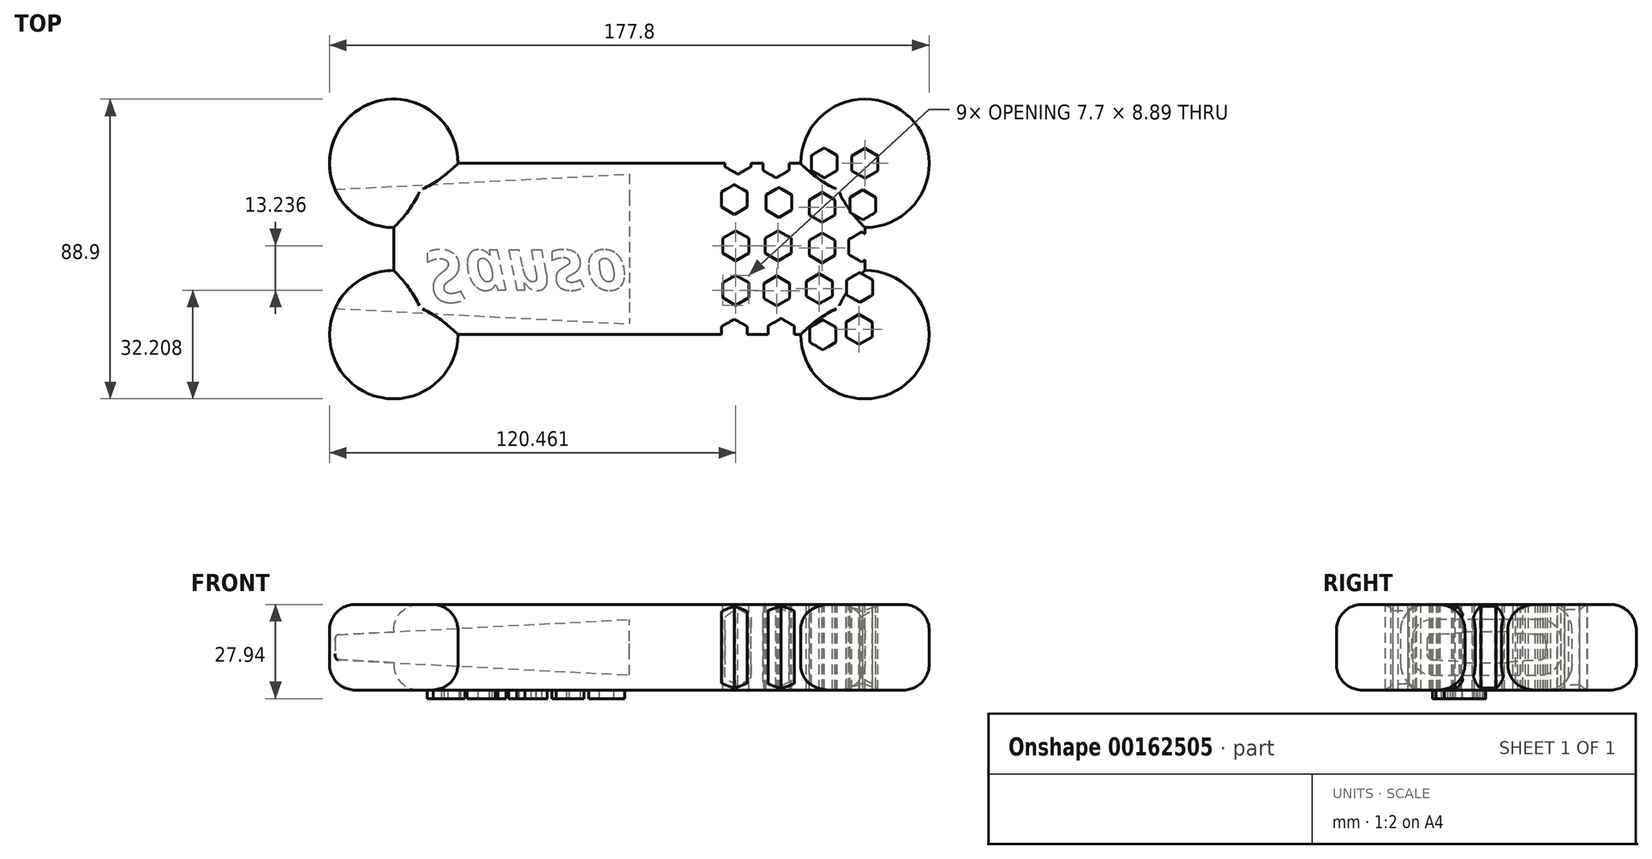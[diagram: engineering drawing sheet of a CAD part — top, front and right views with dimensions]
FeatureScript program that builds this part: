
annotation { "Feature Type Name" : "Feature", "Feature Type Description" : "" }
export const myFeature = defineFeature(function(context is Context, id is Id, definition is map)
    precondition{}
    {
        {
            var Q0;
            Q0=qCreatedBy(makeId("Top.planeOp"),FACE);
            var sketch = newSketch(context, id + "F0", { "sketchPlane" : qUnion([Q0])});
            skLineSegment(sketch, "E0.bottom", {"start": v(-50.8, 25.4) * mm, "end": v(50.8, 25.4) * mm});
            skLineSegment(sketch, "E0.top", {"start": v(-50.8, -25.4) * mm, "end": v(50.8, -25.4) * mm});
            skLineSegment(sketch, "E0.right", {"start": v(69.85, 6.35) * mm, "end": v(69.85, -6.35) * mm});
            skPoint(sketch, "E0.middle", {"position": v(0, 0) * mm});
            skArc(sketch, "E1", {"start": v(-50.8, 25.4) * mm, "mid": v(-83.32, 38.87) * mm, "end": v(-69.85, 6.35) * mm});
            skArc(sketch, "E2", {"start": v(50.8, -25.4) * mm, "mid": v(83.32, -38.87) * mm, "end": v(69.85, -6.35) * mm});
            skArc(sketch, "E3", {"start": v(69.85, 6.35) * mm, "mid": v(83.32, 38.87) * mm, "end": v(50.8, 25.4) * mm});
            skArc(sketch, "E4", {"start": v(-69.85, -6.35) * mm, "mid": v(-83.32, -38.87) * mm, "end": v(-50.8, -25.4) * mm});
            skLineSegment(sketch, "E5", {"start": v(-69.85, 6.35) * mm, "end": v(-69.85, -6.35) * mm});
            skSolve(sketch);
        }
        {
            var Q0;
            Q0 = qSketchRegion(id + "F0", true);
            extrude(context, id + "F1", {"entities" : qUnion([Q0]), "endBound" : BoundingType.SYMMETRIC, "depth" : 25.4 * mm});
        }
        {
            var Q0;
            Q0=makeQuery(id+"F1.opExtrude","CAP_EDGE",EDGE,{"disambiguationData":[OSD([sQuery(id+"F0.wireOp",EDGE,"E4")])],"isStart":false});
            var Q1;
            Q1=makeQuery(id+"F1.opExtrude","CAP_EDGE",EDGE,{"disambiguationData":[OSD([sQuery(id+"F0.wireOp",EDGE,"E5")])],"isStart":false});
            var Q2;
            Q2=makeQuery(id+"F1.opExtrude","CAP_EDGE",EDGE,{"disambiguationData":[OSD([sQuery(id+"F0.wireOp",EDGE,"E1")])],"isStart":false});
            var Q3;
            Q3=makeQuery(id+"F1.opExtrude","CAP_EDGE",EDGE,{"disambiguationData":[OSD([sQuery(id+"F0.wireOp",EDGE,"E4")])],"isStart":true});
            var Q4;
            Q4=makeQuery(id+"F1.opExtrude","CAP_EDGE",EDGE,{"disambiguationData":[OSD([sQuery(id+"F0.wireOp",EDGE,"E5")])],"isStart":true});
            var Q5;
            Q5=makeQuery(id+"F1.opExtrude","CAP_EDGE",EDGE,{"disambiguationData":[OSD([sQuery(id+"F0.wireOp",EDGE,"E1")])],"isStart":true});
            var Q6;
            Q6=makeQuery(id+"F1.opExtrude","CAP_EDGE",EDGE,{"disambiguationData":[OSD([sQuery(id+"F0.wireOp",EDGE,"E0.top")])],"isStart":false});
            var Q7;
            Q7=makeQuery(id+"F1.opExtrude","CAP_EDGE",EDGE,{"disambiguationData":[OSD([sQuery(id+"F0.wireOp",EDGE,"E0.bottom")])],"isStart":false});
            var Q8;
            Q8=makeQuery(id+"F1.opExtrude","CAP_EDGE",EDGE,{"disambiguationData":[OSD([sQuery(id+"F0.wireOp",EDGE,"E2")])],"isStart":false});
            var Q9;
            Q9=makeQuery(id+"F1.opExtrude","CAP_EDGE",EDGE,{"disambiguationData":[OSD([sQuery(id+"F0.wireOp",EDGE,"E0.right")])],"isStart":false});
            var Q10;
            Q10=makeQuery(id+"F1.opExtrude","CAP_EDGE",EDGE,{"disambiguationData":[OSD([sQuery(id+"F0.wireOp",EDGE,"E3")])],"isStart":false});
            var Q11;
            Q11=makeQuery(id+"F1.opExtrude","CAP_EDGE",EDGE,{"disambiguationData":[OSD([sQuery(id+"F0.wireOp",EDGE,"E0.right")])],"isStart":true});
            var Q12;
            Q12=makeQuery(id+"F1.opExtrude","CAP_EDGE",EDGE,{"disambiguationData":[OSD([sQuery(id+"F0.wireOp",EDGE,"E3")])],"isStart":true});
            var Q13;
            Q13=makeQuery(id+"F1.opExtrude","CAP_EDGE",EDGE,{"disambiguationData":[OSD([sQuery(id+"F0.wireOp",EDGE,"E2")])],"isStart":true});
            var Q14;
            Q14=makeQuery(id+"F1.opExtrude","CAP_EDGE",EDGE,{"disambiguationData":[OSD([sQuery(id+"F0.wireOp",EDGE,"E0.top")])],"isStart":true});
            var Q15;
            Q15=makeQuery(id+"F1.opExtrude","CAP_EDGE",EDGE,{"disambiguationData":[OSD([sQuery(id+"F0.wireOp",EDGE,"E0.bottom")])],"isStart":true});
            fillet(context, id + "F2", {"entities" : qUnion([Q0, Q1, Q2, Q3, Q4, Q5, Q6, Q7, Q8, Q9, Q10, Q11, Q12, Q13, Q14, Q15]), "radius" : 7.62 * mm, "tangentPropagation" : true, "allowEdgeOverflow" : false});
        }
        {
            var Q0;
            Q0=qCreatedBy(makeId("Right.planeOp"),FACE);
            var sketch = newSketch(context, id + "F3", { "sketchPlane" : qUnion([Q0])});
            skLineSegment(sketch, "E6.bottom", {"start": v(15.88, 8.26) * mm, "end": v(-15.88, 8.26) * mm});
            skLineSegment(sketch, "E6.top", {"start": v(15.88, -8.26) * mm, "end": v(-15.87, -8.26) * mm});
            skLineSegment(sketch, "E6.left", {"start": v(22.23, 1.9) * mm, "end": v(22.23, -1.9) * mm});
            skLineSegment(sketch, "E6.right", {"start": v(-22.23, 1.9) * mm, "end": v(-22.23, -1.9) * mm});
            skPoint(sketch, "E6.middle", {"position": v(0, 0) * mm});
            skPoint(sketch, "E7.visualSharp", {"position": v(22.23, 8.26) * mm});
            skArc(sketch, "E7.filletArc", {"start": v(22.23, 1.9) * mm, "mid": v(20.37, 6.4) * mm, "end": v(15.88, 8.26) * mm});
            skPoint(sketch, "E8.visualSharp", {"position": v(22.23, -8.26) * mm});
            skArc(sketch, "E8.filletArc", {"start": v(15.88, -8.26) * mm, "mid": v(20.37, -6.4) * mm, "end": v(22.23, -1.9) * mm});
            skPoint(sketch, "E9.visualSharp", {"position": v(-22.23, 8.26) * mm});
            skArc(sketch, "E9.filletArc", {"start": v(-15.88, 8.26) * mm, "mid": v(-20.37, 6.4) * mm, "end": v(-22.23, 1.9) * mm});
            skPoint(sketch, "E10.visualSharp", {"position": v(-22.23, -8.26) * mm});
            skArc(sketch, "E10.filletArc", {"start": v(-22.23, -1.9) * mm, "mid": v(-20.37, -6.4) * mm, "end": v(-15.87, -8.26) * mm});
            skSolve(sketch);
        }
        {
            var Q0;
            Q0 = qSketchRegion(id + "F3", true);
            extrude(context, id + "F4", {"entities" : qUnion([Q0]), "operationType" : NewBodyOperationType.REMOVE, "oppositeDirection" : true, "depth" : 105.16 * mm, "hasDraft" : true, "draftAngle" : 3 * degree, "draftPullDirection" : true});
        }
        {
            var Q0;
            Q0=makeQuery(id+"F1.opExtrude","CAP_FACE",FACE,{"disambiguationData":[OSD([sQuery(id+"F0.wireOp",EDGE,"E0.bottom"),sQuery(id+"F0.wireOp",EDGE,"E0.top"),sQuery(id+"F0.wireOp",EDGE,"E0.right"),sQuery(id+"F0.wireOp",EDGE,"E1"),sQuery(id+"F0.wireOp",EDGE,"E2"),sQuery(id+"F0.wireOp",EDGE,"E3"),sQuery(id+"F0.wireOp",EDGE,"E4"),sQuery(id+"F0.wireOp",EDGE,"E5")])],"isStart":false});
            var sketch = newSketch(context, id + "F5", { "sketchPlane" : qUnion([Q0])});
            skPoint(sketch, "E11", {"position": v(69.85, 25.4) * mm});
            skPoint(sketch, "E12.0.1.0", {"position": v(69.85, 12.7) * mm});
            skPoint(sketch, "E12.0.2.0", {"position": v(69.85, 0) * mm});
            skPoint(sketch, "E12.0.3.0", {"position": v(69.85, -12.7) * mm});
            skPoint(sketch, "E12.0.4.0", {"position": v(69.85, -25.4) * mm});
            skPoint(sketch, "E12.1.0.0", {"position": v(57.15, 25.4) * mm});
            skPoint(sketch, "E12.1.1.0", {"position": v(57.15, 12.7) * mm});
            skPoint(sketch, "E12.1.2.0", {"position": v(57.15, 0) * mm});
            skPoint(sketch, "E12.1.3.0", {"position": v(57.15, -12.7) * mm});
            skPoint(sketch, "E12.1.4.0", {"position": v(57.15, -25.4) * mm});
            skPoint(sketch, "E12.2.0.0", {"position": v(44.45, 25.4) * mm});
            skPoint(sketch, "E12.2.1.0", {"position": v(44.45, 12.7) * mm});
            skPoint(sketch, "E12.2.2.0", {"position": v(44.45, 0) * mm});
            skPoint(sketch, "E12.2.3.0", {"position": v(44.45, -12.7) * mm});
            skPoint(sketch, "E12.2.4.0", {"position": v(44.45, -25.4) * mm});
            skPoint(sketch, "E12.3.0.0", {"position": v(31.75, 25.4) * mm});
            skPoint(sketch, "E12.3.1.0", {"position": v(31.75, 12.7) * mm});
            skPoint(sketch, "E12.3.2.0", {"position": v(31.75, 0) * mm});
            skPoint(sketch, "E12.3.3.0", {"position": v(31.75, -12.7) * mm});
            skPoint(sketch, "E12.3.4.0", {"position": v(31.75, -25.4) * mm});
            skPoint(sketch, "E12.4.0.0", {"position": v(19.05, 25.4) * mm});
            skPoint(sketch, "E12.4.1.0", {"position": v(19.05, 12.7) * mm});
            skPoint(sketch, "E12.4.2.0", {"position": v(19.05, 0) * mm});
            skPoint(sketch, "E12.4.3.0", {"position": v(19.05, -12.7) * mm});
            skPoint(sketch, "E12.4.4.0", {"position": v(19.05, -25.4) * mm});
            skPoint(sketch, "E12.5.0.0", {"position": v(6.35, 25.4) * mm});
            skPoint(sketch, "E12.5.1.0", {"position": v(6.35, 12.7) * mm});
            skPoint(sketch, "E12.5.2.0", {"position": v(6.35, 0) * mm});
            skPoint(sketch, "E12.5.3.0", {"position": v(6.35, -12.7) * mm});
            skPoint(sketch, "E12.5.4.0", {"position": v(6.35, -25.4) * mm});
            skPoint(sketch, "E12.6.0.0", {"position": v(-6.35, 25.4) * mm});
            skPoint(sketch, "E12.6.1.0", {"position": v(-6.35, 12.7) * mm});
            skPoint(sketch, "E12.6.2.0", {"position": v(-6.35, 0) * mm});
            skPoint(sketch, "E12.6.3.0", {"position": v(-6.35, -12.7) * mm});
            skPoint(sketch, "E12.6.4.0", {"position": v(-6.35, -25.4) * mm});
            skLineSegment(sketch, "E12.direction1", {"start": v(69.85, 25.4) * mm, "end": v(57.15, 25.4) * mm, "construction": true});
            skLineSegment(sketch, "E12.direction2", {"start": v(69.85, 25.4) * mm, "end": v(69.85, 12.7) * mm, "construction": true});
            skCircle(sketch, "E13.cCircle", {"center": v(69.85, 25.4) * mm, "radius": 3.85 * mm, "construction": true});
            skLineSegment(sketch, "E13.0", {"start": v(73.7, 27.62) * mm, "end": v(73.7, 23.18) * mm});
            skLineSegment(sketch, "E13.1", {"start": v(73.7, 23.18) * mm, "end": v(69.85, 20.96) * mm});
            skLineSegment(sketch, "E13.2", {"start": v(69.85, 20.96) * mm, "end": v(66, 23.18) * mm});
            skLineSegment(sketch, "E13.3", {"start": v(66, 23.18) * mm, "end": v(66, 27.62) * mm});
            skLineSegment(sketch, "E13.4", {"start": v(66, 27.62) * mm, "end": v(69.85, 29.85) * mm});
            skLineSegment(sketch, "E13.5", {"start": v(69.85, 29.84) * mm, "end": v(73.7, 27.62) * mm});
            skPoint(sketch, "E13.0.midPoint", {"position": v(73.7, 25.4) * mm});
            skPoint(sketch, "E14", {"position": v(69.22, 13.1) * mm});
            skLineSegment(sketch, "E15.direction1", {"start": v(69.22, 13.1) * mm, "end": v(56.52, 13.1) * mm, "construction": true});
            skLineSegment(sketch, "E15.direction2", {"start": v(69.22, 13.1) * mm, "end": v(69.22, 0.4) * mm, "construction": true});
            skCircle(sketch, "E16.cCircle", {"center": v(69.22, 13.1) * mm, "radius": 3.85 * mm, "construction": true});
            skLineSegment(sketch, "E16.0", {"start": v(73.07, 15.33) * mm, "end": v(73.07, 10.88) * mm});
            skLineSegment(sketch, "E16.1", {"start": v(73.07, 10.88) * mm, "end": v(69.22, 8.66) * mm});
            skLineSegment(sketch, "E16.2", {"start": v(69.22, 8.66) * mm, "end": v(65.37, 10.88) * mm});
            skLineSegment(sketch, "E16.3", {"start": v(65.37, 10.88) * mm, "end": v(65.37, 15.33) * mm});
            skLineSegment(sketch, "E16.4", {"start": v(65.37, 15.33) * mm, "end": v(69.22, 17.55) * mm});
            skLineSegment(sketch, "E16.5", {"start": v(69.22, 17.55) * mm, "end": v(73.07, 15.33) * mm});
            skPoint(sketch, "E16.0.midPoint", {"position": v(73.07, 13.1) * mm});
            skPoint(sketch, "E17", {"position": v(68.9, 0.6) * mm});
            skLineSegment(sketch, "E18.direction1", {"start": v(68.9, 0.6) * mm, "end": v(56.2, 0.6) * mm, "construction": true});
            skLineSegment(sketch, "E18.direction2", {"start": v(68.9, 0.6) * mm, "end": v(68.9, -12.1) * mm, "construction": true});
            skCircle(sketch, "E19.cCircle", {"center": v(68.9, 0.6) * mm, "radius": 3.85 * mm, "construction": true});
            skLineSegment(sketch, "E19.0", {"start": v(72.75, 2.82) * mm, "end": v(72.75, -1.63) * mm});
            skLineSegment(sketch, "E19.1", {"start": v(72.75, -1.63) * mm, "end": v(68.9, -3.85) * mm});
            skLineSegment(sketch, "E19.2", {"start": v(68.9, -3.85) * mm, "end": v(65.05, -1.63) * mm});
            skLineSegment(sketch, "E19.3", {"start": v(65.05, -1.63) * mm, "end": v(65.05, 2.82) * mm});
            skLineSegment(sketch, "E19.4", {"start": v(65.05, 2.82) * mm, "end": v(68.9, 5.04) * mm});
            skLineSegment(sketch, "E19.5", {"start": v(68.9, 5.04) * mm, "end": v(72.75, 2.82) * mm});
            skPoint(sketch, "E19.0.midPoint", {"position": v(72.75, 0.6) * mm});
            skPoint(sketch, "E20", {"position": v(68.32, -11.42) * mm});
            skLineSegment(sketch, "E21.direction1", {"start": v(68.32, -11.42) * mm, "end": v(55.62, -11.42) * mm, "construction": true});
            skLineSegment(sketch, "E21.direction2", {"start": v(68.32, -11.42) * mm, "end": v(68.32, -24.12) * mm, "construction": true});
            skCircle(sketch, "E22.cCircle", {"center": v(68.32, -11.42) * mm, "radius": 3.85 * mm, "construction": true});
            skLineSegment(sketch, "E22.0", {"start": v(72.17, -9.2) * mm, "end": v(72.17, -13.64) * mm});
            skLineSegment(sketch, "E22.1", {"start": v(72.17, -13.64) * mm, "end": v(68.32, -15.86) * mm});
            skLineSegment(sketch, "E22.2", {"start": v(68.32, -15.86) * mm, "end": v(64.47, -13.64) * mm});
            skLineSegment(sketch, "E22.3", {"start": v(64.47, -13.64) * mm, "end": v(64.47, -9.2) * mm});
            skLineSegment(sketch, "E22.4", {"start": v(64.47, -9.2) * mm, "end": v(68.32, -6.97) * mm});
            skLineSegment(sketch, "E22.5", {"start": v(68.32, -6.97) * mm, "end": v(72.17, -9.2) * mm});
            skPoint(sketch, "E22.0.midPoint", {"position": v(72.17, -11.42) * mm});
            skPoint(sketch, "E23", {"position": v(68.12, -23.85) * mm});
            skLineSegment(sketch, "E24.direction1", {"start": v(68.12, -23.85) * mm, "end": v(55.42, -23.85) * mm, "construction": true});
            skLineSegment(sketch, "E24.direction2", {"start": v(68.12, -23.85) * mm, "end": v(68.12, -36.55) * mm, "construction": true});
            skCircle(sketch, "E25.cCircle", {"center": v(68.12, -23.85) * mm, "radius": 3.85 * mm, "construction": true});
            skLineSegment(sketch, "E25.0", {"start": v(71.97, -21.63) * mm, "end": v(71.97, -26.07) * mm});
            skLineSegment(sketch, "E25.1", {"start": v(71.97, -26.07) * mm, "end": v(68.12, -28.3) * mm});
            skLineSegment(sketch, "E25.2", {"start": v(68.12, -28.3) * mm, "end": v(64.27, -26.07) * mm});
            skLineSegment(sketch, "E25.3", {"start": v(64.27, -26.07) * mm, "end": v(64.27, -21.63) * mm});
            skLineSegment(sketch, "E25.4", {"start": v(64.27, -21.63) * mm, "end": v(68.12, -19.4) * mm});
            skLineSegment(sketch, "E25.5", {"start": v(68.12, -19.4) * mm, "end": v(71.97, -21.63) * mm});
            skPoint(sketch, "E25.0.midPoint", {"position": v(71.97, -23.85) * mm});
            skPoint(sketch, "E26", {"position": v(57.82, 25.54) * mm});
            skLineSegment(sketch, "E27.direction1", {"start": v(57.82, 25.54) * mm, "end": v(45.12, 25.54) * mm, "construction": true});
            skLineSegment(sketch, "E27.direction2", {"start": v(57.82, 25.54) * mm, "end": v(57.82, 12.84) * mm, "construction": true});
            skCircle(sketch, "E28.cCircle", {"center": v(57.82, 25.54) * mm, "radius": 3.85 * mm, "construction": true});
            skLineSegment(sketch, "E28.0", {"start": v(61.67, 27.77) * mm, "end": v(61.67, 23.32) * mm});
            skLineSegment(sketch, "E28.1", {"start": v(61.67, 23.32) * mm, "end": v(57.82, 21.1) * mm});
            skLineSegment(sketch, "E28.2", {"start": v(57.82, 21.1) * mm, "end": v(53.97, 23.32) * mm});
            skLineSegment(sketch, "E28.3", {"start": v(53.97, 23.32) * mm, "end": v(53.97, 27.77) * mm});
            skLineSegment(sketch, "E28.4", {"start": v(53.97, 27.77) * mm, "end": v(57.82, 29.99) * mm});
            skLineSegment(sketch, "E28.5", {"start": v(57.82, 29.99) * mm, "end": v(61.67, 27.77) * mm});
            skPoint(sketch, "E28.0.midPoint", {"position": v(61.67, 25.54) * mm});
            skPoint(sketch, "E29", {"position": v(57.18, 12.3) * mm});
            skLineSegment(sketch, "E30.direction1", {"start": v(57.18, 12.3) * mm, "end": v(44.48, 12.3) * mm, "construction": true});
            skLineSegment(sketch, "E30.direction2", {"start": v(57.18, 12.3) * mm, "end": v(57.18, -0.4) * mm, "construction": true});
            skCircle(sketch, "E31.cCircle", {"center": v(57.18, 12.3) * mm, "radius": 3.85 * mm, "construction": true});
            skLineSegment(sketch, "E31.0", {"start": v(61.03, 14.53) * mm, "end": v(61.03, 10.09) * mm});
            skLineSegment(sketch, "E31.1", {"start": v(61.03, 10.09) * mm, "end": v(57.18, 7.86) * mm});
            skLineSegment(sketch, "E31.2", {"start": v(57.18, 7.86) * mm, "end": v(53.33, 10.09) * mm});
            skLineSegment(sketch, "E31.3", {"start": v(53.33, 10.09) * mm, "end": v(53.33, 14.53) * mm});
            skLineSegment(sketch, "E31.4", {"start": v(53.33, 14.53) * mm, "end": v(57.18, 16.75) * mm});
            skLineSegment(sketch, "E31.5", {"start": v(57.18, 16.75) * mm, "end": v(61.03, 14.53) * mm});
            skPoint(sketch, "E31.0.midPoint", {"position": v(61.03, 12.3) * mm});
            skPoint(sketch, "E32", {"position": v(57.18, 0.35) * mm});
            skLineSegment(sketch, "E33.direction1", {"start": v(57.18, 0.35) * mm, "end": v(44.48, 0.35) * mm, "construction": true});
            skLineSegment(sketch, "E33.direction2", {"start": v(57.18, 0.35) * mm, "end": v(57.18, -12.35) * mm, "construction": true});
            skCircle(sketch, "E34.cCircle", {"center": v(57.18, 0.35) * mm, "radius": 3.85 * mm, "construction": true});
            skLineSegment(sketch, "E34.0", {"start": v(61.03, 2.58) * mm, "end": v(61.03, -1.87) * mm});
            skLineSegment(sketch, "E34.1", {"start": v(61.03, -1.87) * mm, "end": v(57.18, -4.1) * mm});
            skLineSegment(sketch, "E34.2", {"start": v(57.18, -4.1) * mm, "end": v(53.33, -1.87) * mm});
            skLineSegment(sketch, "E34.3", {"start": v(53.33, -1.87) * mm, "end": v(53.33, 2.58) * mm});
            skLineSegment(sketch, "E34.4", {"start": v(53.33, 2.58) * mm, "end": v(57.18, 4.8) * mm});
            skLineSegment(sketch, "E34.5", {"start": v(57.18, 4.8) * mm, "end": v(61.03, 2.58) * mm});
            skPoint(sketch, "E34.0.midPoint", {"position": v(61.03, 0.35) * mm});
            skPoint(sketch, "E35", {"position": v(56.32, -11.82) * mm});
            skLineSegment(sketch, "E36.direction1", {"start": v(56.32, -11.82) * mm, "end": v(43.62, -11.82) * mm, "construction": true});
            skLineSegment(sketch, "E36.direction2", {"start": v(56.32, -11.82) * mm, "end": v(56.32, -24.52) * mm, "construction": true});
            skCircle(sketch, "E37.cCircle", {"center": v(56.32, -11.82) * mm, "radius": 3.85 * mm, "construction": true});
            skLineSegment(sketch, "E37.0", {"start": v(60.17, -9.6) * mm, "end": v(60.17, -14.04) * mm});
            skLineSegment(sketch, "E37.1", {"start": v(60.17, -14.04) * mm, "end": v(56.32, -16.26) * mm});
            skLineSegment(sketch, "E37.2", {"start": v(56.32, -16.26) * mm, "end": v(52.48, -14.04) * mm});
            skLineSegment(sketch, "E37.3", {"start": v(52.48, -14.04) * mm, "end": v(52.48, -9.6) * mm});
            skLineSegment(sketch, "E37.4", {"start": v(52.48, -9.6) * mm, "end": v(56.32, -7.37) * mm});
            skLineSegment(sketch, "E37.5", {"start": v(56.32, -7.37) * mm, "end": v(60.17, -9.6) * mm});
            skPoint(sketch, "E37.0.midPoint", {"position": v(60.17, -11.82) * mm});
            skPoint(sketch, "E38", {"position": v(57.4, -25.48) * mm});
            skLineSegment(sketch, "E39.direction1", {"start": v(57.4, -25.48) * mm, "end": v(44.7, -25.48) * mm, "construction": true});
            skLineSegment(sketch, "E39.direction2", {"start": v(57.4, -25.48) * mm, "end": v(57.4, -38.18) * mm, "construction": true});
            skCircle(sketch, "E40.cCircle", {"center": v(57.4, -25.48) * mm, "radius": 3.85 * mm, "construction": true});
            skLineSegment(sketch, "E40.0", {"start": v(61.24, -23.26) * mm, "end": v(61.24, -27.7) * mm});
            skLineSegment(sketch, "E40.1", {"start": v(61.24, -27.7) * mm, "end": v(57.4, -29.92) * mm});
            skLineSegment(sketch, "E40.2", {"start": v(57.4, -29.92) * mm, "end": v(53.54, -27.7) * mm});
            skLineSegment(sketch, "E40.3", {"start": v(53.54, -27.7) * mm, "end": v(53.54, -23.26) * mm});
            skLineSegment(sketch, "E40.4", {"start": v(53.54, -23.26) * mm, "end": v(57.4, -21.03) * mm});
            skLineSegment(sketch, "E40.5", {"start": v(57.4, -21.03) * mm, "end": v(61.24, -23.26) * mm});
            skPoint(sketch, "E40.0.midPoint", {"position": v(61.24, -25.48) * mm});
            skPoint(sketch, "E41", {"position": v(45.01, -25.05) * mm});
            skLineSegment(sketch, "E42.direction1", {"start": v(45.01, -25.05) * mm, "end": v(32.31, -25.05) * mm, "construction": true});
            skLineSegment(sketch, "E42.direction2", {"start": v(45.01, -25.05) * mm, "end": v(45.01, -37.75) * mm, "construction": true});
            skCircle(sketch, "E43.cCircle", {"center": v(45.01, -25.05) * mm, "radius": 3.85 * mm, "construction": true});
            skLineSegment(sketch, "E43.0", {"start": v(48.86, -22.83) * mm, "end": v(48.86, -27.27) * mm});
            skLineSegment(sketch, "E43.1", {"start": v(48.86, -27.27) * mm, "end": v(45.01, -29.5) * mm});
            skLineSegment(sketch, "E43.2", {"start": v(45.01, -29.5) * mm, "end": v(41.16, -27.27) * mm});
            skLineSegment(sketch, "E43.3", {"start": v(41.16, -27.27) * mm, "end": v(41.16, -22.83) * mm});
            skLineSegment(sketch, "E43.4", {"start": v(41.16, -22.83) * mm, "end": v(45.01, -20.6) * mm});
            skLineSegment(sketch, "E43.5", {"start": v(45.01, -20.6) * mm, "end": v(48.86, -22.83) * mm});
            skPoint(sketch, "E43.0.midPoint", {"position": v(48.86, -25.05) * mm});
            skPoint(sketch, "E44", {"position": v(43.73, -12.46) * mm});
            skLineSegment(sketch, "E45.direction1", {"start": v(43.73, -12.46) * mm, "end": v(31.03, -12.46) * mm, "construction": true});
            skLineSegment(sketch, "E45.direction2", {"start": v(43.73, -12.46) * mm, "end": v(43.73, -25.16) * mm, "construction": true});
            skCircle(sketch, "E46.cCircle", {"center": v(43.73, -12.46) * mm, "radius": 3.85 * mm, "construction": true});
            skLineSegment(sketch, "E46.0", {"start": v(47.58, -10.23) * mm, "end": v(47.58, -14.68) * mm});
            skLineSegment(sketch, "E46.1", {"start": v(47.58, -14.68) * mm, "end": v(43.73, -16.9) * mm});
            skLineSegment(sketch, "E46.2", {"start": v(43.73, -16.9) * mm, "end": v(39.88, -14.68) * mm});
            skLineSegment(sketch, "E46.3", {"start": v(39.88, -14.68) * mm, "end": v(39.88, -10.23) * mm});
            skLineSegment(sketch, "E46.4", {"start": v(39.88, -10.23) * mm, "end": v(43.73, -8.01) * mm});
            skLineSegment(sketch, "E46.5", {"start": v(43.73, -8.01) * mm, "end": v(47.58, -10.23) * mm});
            skPoint(sketch, "E46.0.midPoint", {"position": v(47.58, -12.46) * mm});
            skPoint(sketch, "E47", {"position": v(44.16, 1) * mm});
            skLineSegment(sketch, "E48.direction1", {"start": v(44.16, 1) * mm, "end": v(31.46, 1) * mm, "construction": true});
            skLineSegment(sketch, "E48.direction2", {"start": v(44.16, 1) * mm, "end": v(44.16, -11.7) * mm, "construction": true});
            skCircle(sketch, "E49.cCircle", {"center": v(44.16, 1) * mm, "radius": 3.85 * mm, "construction": true});
            skLineSegment(sketch, "E49.0", {"start": v(48, 3.22) * mm, "end": v(48, -1.23) * mm});
            skLineSegment(sketch, "E49.1", {"start": v(48, -1.23) * mm, "end": v(44.16, -3.45) * mm});
            skLineSegment(sketch, "E49.2", {"start": v(44.16, -3.45) * mm, "end": v(40.3, -1.23) * mm});
            skLineSegment(sketch, "E49.3", {"start": v(40.3, -1.23) * mm, "end": v(40.3, 3.22) * mm});
            skLineSegment(sketch, "E49.4", {"start": v(40.3, 3.22) * mm, "end": v(44.16, 5.44) * mm});
            skLineSegment(sketch, "E49.5", {"start": v(44.16, 5.44) * mm, "end": v(48, 3.22) * mm});
            skPoint(sketch, "E49.0.midPoint", {"position": v(48, 1) * mm});
            skPoint(sketch, "E50", {"position": v(44.37, 13.8) * mm});
            skLineSegment(sketch, "E51.direction1", {"start": v(44.37, 13.8) * mm, "end": v(31.67, 13.8) * mm, "construction": true});
            skLineSegment(sketch, "E51.direction2", {"start": v(44.37, 13.8) * mm, "end": v(44.37, 1.1) * mm, "construction": true});
            skCircle(sketch, "E52.cCircle", {"center": v(44.37, 13.8) * mm, "radius": 3.85 * mm, "construction": true});
            skLineSegment(sketch, "E52.0", {"start": v(48.22, 16.02) * mm, "end": v(48.22, 11.58) * mm});
            skLineSegment(sketch, "E52.1", {"start": v(48.22, 11.58) * mm, "end": v(44.37, 9.36) * mm});
            skLineSegment(sketch, "E52.2", {"start": v(44.37, 9.36) * mm, "end": v(40.52, 11.58) * mm});
            skLineSegment(sketch, "E52.3", {"start": v(40.52, 11.58) * mm, "end": v(40.52, 16.02) * mm});
            skLineSegment(sketch, "E52.4", {"start": v(40.52, 16.02) * mm, "end": v(44.37, 18.25) * mm});
            skLineSegment(sketch, "E52.5", {"start": v(44.37, 18.25) * mm, "end": v(48.22, 16.02) * mm});
            skPoint(sketch, "E52.0.midPoint", {"position": v(48.22, 13.8) * mm});
            skPoint(sketch, "E53", {"position": v(43.52, 25.54) * mm});
            skLineSegment(sketch, "E54.direction1", {"start": v(43.52, 25.54) * mm, "end": v(30.82, 25.54) * mm, "construction": true});
            skLineSegment(sketch, "E54.direction2", {"start": v(43.52, 25.54) * mm, "end": v(43.52, 12.84) * mm, "construction": true});
            skCircle(sketch, "E55.cCircle", {"center": v(43.52, 25.54) * mm, "radius": 3.85 * mm, "construction": true});
            skLineSegment(sketch, "E55.0", {"start": v(47.37, 27.77) * mm, "end": v(47.37, 23.32) * mm});
            skLineSegment(sketch, "E55.1", {"start": v(47.37, 23.32) * mm, "end": v(43.52, 21.1) * mm});
            skLineSegment(sketch, "E55.2", {"start": v(43.52, 21.1) * mm, "end": v(39.67, 23.32) * mm});
            skLineSegment(sketch, "E55.3", {"start": v(39.67, 23.32) * mm, "end": v(39.67, 27.77) * mm});
            skLineSegment(sketch, "E55.4", {"start": v(39.67, 27.77) * mm, "end": v(43.52, 29.99) * mm});
            skLineSegment(sketch, "E55.5", {"start": v(43.52, 29.99) * mm, "end": v(47.37, 27.77) * mm});
            skPoint(sketch, "E55.0.midPoint", {"position": v(47.37, 25.54) * mm});
            skPoint(sketch, "E56", {"position": v(32.2, 26.61) * mm});
            skLineSegment(sketch, "E57.direction1", {"start": v(32.2, 26.61) * mm, "end": v(19.5, 26.61) * mm, "construction": true});
            skLineSegment(sketch, "E57.direction2", {"start": v(32.2, 26.61) * mm, "end": v(32.2, 13.91) * mm, "construction": true});
            skCircle(sketch, "E58.cCircle", {"center": v(32.2, 26.61) * mm, "radius": 3.85 * mm, "construction": true});
            skLineSegment(sketch, "E58.0", {"start": v(36.05, 28.83) * mm, "end": v(36.05, 24.39) * mm});
            skLineSegment(sketch, "E58.1", {"start": v(36.05, 24.39) * mm, "end": v(32.2, 22.17) * mm});
            skLineSegment(sketch, "E58.2", {"start": v(32.2, 22.17) * mm, "end": v(28.35, 24.39) * mm});
            skLineSegment(sketch, "E58.3", {"start": v(28.35, 24.39) * mm, "end": v(28.35, 28.83) * mm});
            skLineSegment(sketch, "E58.4", {"start": v(28.35, 28.83) * mm, "end": v(32.2, 31.06) * mm});
            skLineSegment(sketch, "E58.5", {"start": v(32.2, 31.06) * mm, "end": v(36.05, 28.83) * mm});
            skPoint(sketch, "E58.0.midPoint", {"position": v(36.05, 26.61) * mm});
            skPoint(sketch, "E59", {"position": v(31.13, 14.66) * mm});
            skLineSegment(sketch, "E60.direction1", {"start": v(31.13, 14.66) * mm, "end": v(18.43, 14.66) * mm, "construction": true});
            skLineSegment(sketch, "E60.direction2", {"start": v(31.13, 14.66) * mm, "end": v(31.13, 1.96) * mm, "construction": true});
            skCircle(sketch, "E61.cCircle", {"center": v(31.13, 14.66) * mm, "radius": 3.85 * mm, "construction": true});
            skLineSegment(sketch, "E61.0", {"start": v(34.98, 16.88) * mm, "end": v(34.98, 12.43) * mm});
            skLineSegment(sketch, "E61.1", {"start": v(34.98, 12.43) * mm, "end": v(31.13, 10.21) * mm});
            skLineSegment(sketch, "E61.2", {"start": v(31.13, 10.21) * mm, "end": v(27.28, 12.43) * mm});
            skLineSegment(sketch, "E61.3", {"start": v(27.28, 12.43) * mm, "end": v(27.28, 16.88) * mm});
            skLineSegment(sketch, "E61.4", {"start": v(27.28, 16.88) * mm, "end": v(31.13, 19.1) * mm});
            skLineSegment(sketch, "E61.5", {"start": v(31.13, 19.1) * mm, "end": v(34.98, 16.88) * mm});
            skPoint(sketch, "E61.0.midPoint", {"position": v(34.98, 14.66) * mm});
            skPoint(sketch, "E62", {"position": v(31.56, 1) * mm});
            skLineSegment(sketch, "E63.direction1", {"start": v(31.56, 1) * mm, "end": v(18.86, 1) * mm, "construction": true});
            skLineSegment(sketch, "E63.direction2", {"start": v(31.56, 1) * mm, "end": v(31.56, -11.7) * mm, "construction": true});
            skCircle(sketch, "E64.cCircle", {"center": v(31.56, 1) * mm, "radius": 3.85 * mm, "construction": true});
            skLineSegment(sketch, "E64.0", {"start": v(35.41, 3.22) * mm, "end": v(35.41, -1.23) * mm});
            skLineSegment(sketch, "E64.1", {"start": v(35.41, -1.23) * mm, "end": v(31.56, -3.45) * mm});
            skLineSegment(sketch, "E64.2", {"start": v(31.56, -3.45) * mm, "end": v(27.71, -1.23) * mm});
            skLineSegment(sketch, "E64.3", {"start": v(27.71, -1.23) * mm, "end": v(27.71, 3.22) * mm});
            skLineSegment(sketch, "E64.4", {"start": v(27.71, 3.22) * mm, "end": v(31.56, 5.44) * mm});
            skLineSegment(sketch, "E64.5", {"start": v(31.56, 5.44) * mm, "end": v(35.41, 3.22) * mm});
            skPoint(sketch, "E64.0.midPoint", {"position": v(35.41, 1) * mm});
            skPoint(sketch, "E65", {"position": v(31.56, -12.24) * mm});
            skLineSegment(sketch, "E66.direction1", {"start": v(31.56, -12.24) * mm, "end": v(18.86, -12.24) * mm, "construction": true});
            skLineSegment(sketch, "E66.direction2", {"start": v(31.56, -12.24) * mm, "end": v(31.56, -24.94) * mm, "construction": true});
            skCircle(sketch, "E67.cCircle", {"center": v(31.56, -12.24) * mm, "radius": 3.85 * mm, "construction": true});
            skLineSegment(sketch, "E67.0", {"start": v(35.41, -10.02) * mm, "end": v(35.41, -14.46) * mm});
            skLineSegment(sketch, "E67.1", {"start": v(35.41, -14.46) * mm, "end": v(31.56, -16.69) * mm});
            skLineSegment(sketch, "E67.2", {"start": v(31.56, -16.69) * mm, "end": v(27.71, -14.46) * mm});
            skLineSegment(sketch, "E67.3", {"start": v(27.71, -14.46) * mm, "end": v(27.71, -10.02) * mm});
            skLineSegment(sketch, "E67.4", {"start": v(27.71, -10.02) * mm, "end": v(31.56, -7.8) * mm});
            skLineSegment(sketch, "E67.5", {"start": v(31.56, -7.8) * mm, "end": v(35.41, -10.02) * mm});
            skPoint(sketch, "E67.0.midPoint", {"position": v(35.41, -12.24) * mm});
            skPoint(sketch, "E68", {"position": v(31.13, -25.26) * mm});
            skLineSegment(sketch, "E69.direction1", {"start": v(31.13, -25.26) * mm, "end": v(18.43, -25.26) * mm, "construction": true});
            skLineSegment(sketch, "E69.direction2", {"start": v(31.13, -25.26) * mm, "end": v(31.13, -37.96) * mm, "construction": true});
            skCircle(sketch, "E70.cCircle", {"center": v(31.13, -25.26) * mm, "radius": 3.85 * mm, "construction": true});
            skLineSegment(sketch, "E70.0", {"start": v(34.98, -23.04) * mm, "end": v(34.98, -27.49) * mm});
            skLineSegment(sketch, "E70.1", {"start": v(34.98, -27.49) * mm, "end": v(31.13, -29.7) * mm});
            skLineSegment(sketch, "E70.2", {"start": v(31.13, -29.7) * mm, "end": v(27.28, -27.49) * mm});
            skLineSegment(sketch, "E70.3", {"start": v(27.28, -27.49) * mm, "end": v(27.28, -23.04) * mm});
            skLineSegment(sketch, "E70.4", {"start": v(27.28, -23.04) * mm, "end": v(31.13, -20.82) * mm});
            skLineSegment(sketch, "E70.5", {"start": v(31.13, -20.82) * mm, "end": v(34.98, -23.04) * mm});
            skPoint(sketch, "E70.0.midPoint", {"position": v(34.98, -25.26) * mm});
            skSolve(sketch);
        }
        {
            var Q0;
            Q0 = qSketchRegion(id + "F5", true);
            extrude(context, id + "F6", {"entities" : qUnion([Q0]), "operationType" : NewBodyOperationType.REMOVE, "oppositeDirection" : true, "depth" : 41.4 * mm});
        }
        {
            var Q0;
            Q0=makeQuery(id+"F1.opExtrude","CAP_FACE",FACE,{"disambiguationData":[OSD([sQuery(id+"F0.wireOp",EDGE,"E0.bottom"),sQuery(id+"F0.wireOp",EDGE,"E0.top"),sQuery(id+"F0.wireOp",EDGE,"E0.right"),sQuery(id+"F0.wireOp",EDGE,"E1"),sQuery(id+"F0.wireOp",EDGE,"E2"),sQuery(id+"F0.wireOp",EDGE,"E3"),sQuery(id+"F0.wireOp",EDGE,"E4"),sQuery(id+"F0.wireOp",EDGE,"E5")])],"isStart":true});
            var sketch = newSketch(context, id + "F7", { "sketchPlane" : qUnion([Q0])});
            skText(sketch, "E71", { "text": "Sanso", "fontName": "OpenSans-BoldItalic.ttf"});
            const initialGuessF7  = {"E71": [-0.06039, 0.00038, 1, 0, 0.01549]};
            skSetInitialGuess(sketch, initialGuessF7);
            skSolve(sketch);
        }
        {
            var Q0;
            Q0 = qSketchRegion(id + "F7", true);
            extrude(context, id + "F8", {"entities" : qUnion([Q0]), "operationType" : NewBodyOperationType.ADD, "depth" : 2.54 * mm});
        }
    });
